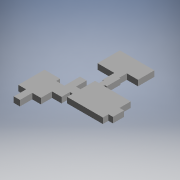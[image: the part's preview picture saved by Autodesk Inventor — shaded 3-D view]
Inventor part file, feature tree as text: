
AUTODESK INVENTOR PART (.ipt)
format: ipt  version: 2019.4 (Build 234330000, 330)  size: 141,824 bytes
history: native  units: mm (DEFAULTED — no unit token found)
features: extrude x1, sketch x1
ambient origin geometry x8: Origin, YZ Plane, XZ Plane, XY Plane, X Axis, Y Axis, Z Axis, Center Point
bodies: Solid1 (feature_tree)
feature tree (2):
  extrude  "Extrusion1"  Depth=800.0mm
  sketch  "Sketch1"  dims[d0=2000.0mm d1=800.0mm d2=1000.0mm d3=6400.0mm d4=1000.0mm d5=1400.0mm d6=2000.0mm d7=700.0mm d8=800.0mm d9=500.0mm d10=1500.0mm d11=1700.0mm d12=2000.0mm d13=1550.0mm d14=1100.0mm d15=800.0mm d16=1900.0mm d17=1200.0mm d18=2800.0mm d19=1450.0mm d20=700.0mm d21=2800.0mm d22=2200.0mm d23=850.0mm d24=200.0mm d25=2100.0mm d26=3000.0mm d27=4000.0mm d28=200.0mm d29=400.0mm d30=2450.0mm d31=200.0mm d32=1350.0mm d33=2000.0mm d34=1000.0mm d35=0.0mm]
